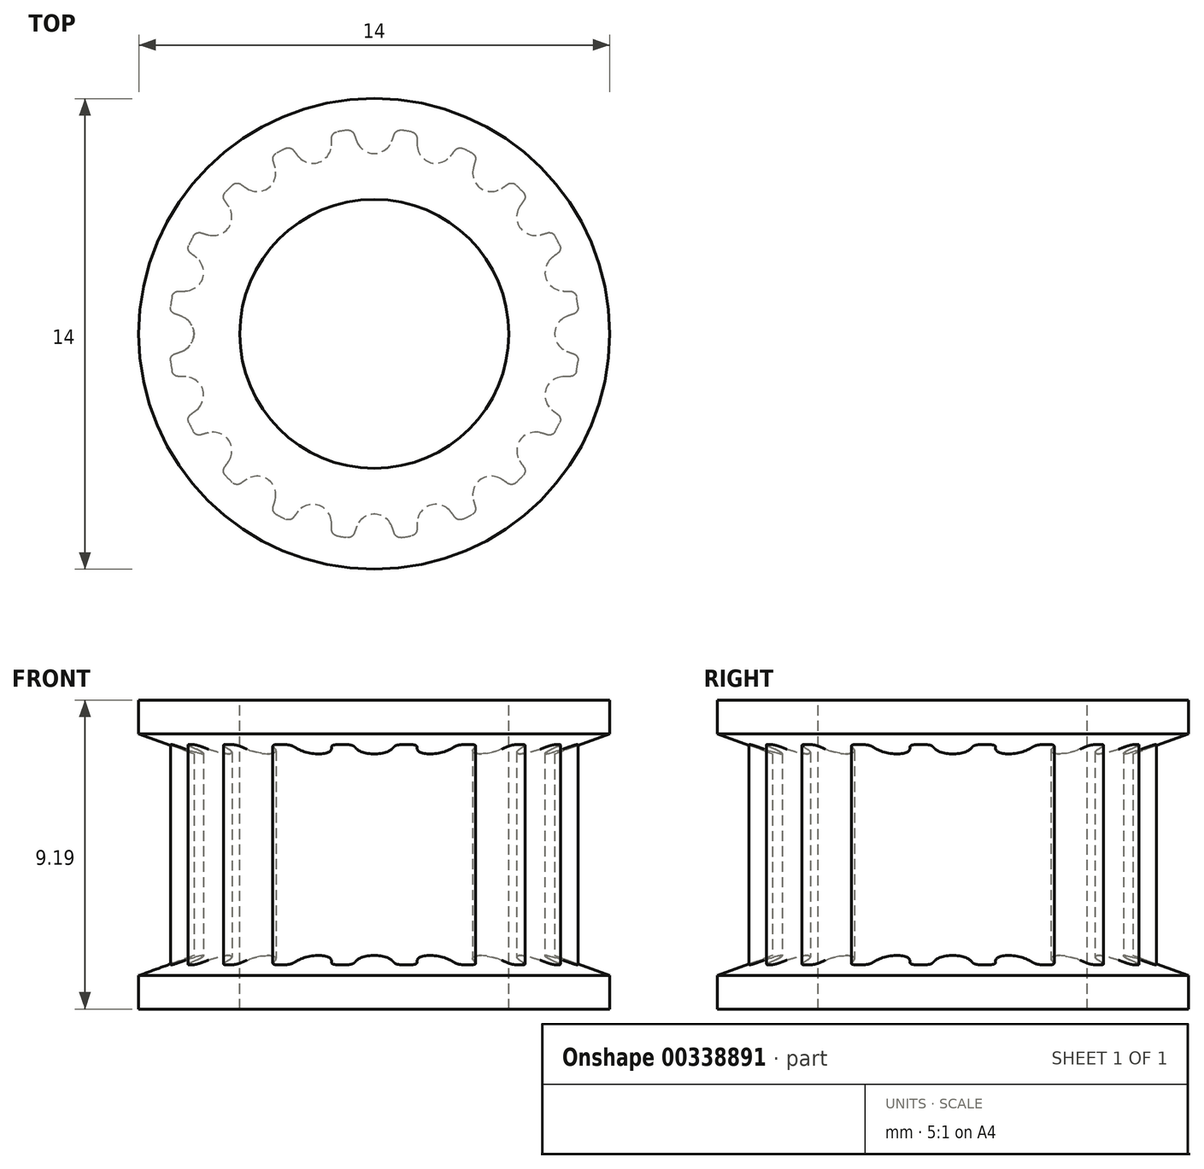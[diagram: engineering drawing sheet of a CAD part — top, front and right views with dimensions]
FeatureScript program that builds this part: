
annotation { "Feature Type Name" : "Feature", "Feature Type Description" : "" }
export const myFeature = defineFeature(function(context is Context, id is Id, definition is map)
    precondition{}
    {
        {
            assignVariable(context, id + "F0", {"name" : "teeth", "anyValue" : 20});
        }
        {
            assignVariable(context, id + "F1", {"name" : "total_length", "anyValue" : 9});
        }
        {
            var Q0;
            Q0=qCreatedBy(makeId("Top.planeOp"),FACE);
            var sketch = newSketch(context, id + "F2", { "sketchPlane" : qUnion([Q0])});
            skLineSegment(sketch, "E0", {"start": v(0, 0) * mm, "end": v(0, 5.36) * mm, "construction": true});
            skCircle(sketch, "E1", {"center": v(0, 0) * mm, "radius": 6.11 * mm});
            skPoint(sketch, "E2.MirrorCS.end.orphan", {"position": v(0.96, 6.04) * mm});
            skLineSegment(sketch, "E3", {"start": v(0.96, 6.04) * mm, "end": v(1, 6.29) * mm, "construction": true});
            skLineSegment(sketch, "E4", {"start": v(-0.96, 6.04) * mm, "end": v(-1, 6.29) * mm, "construction": true});
            skArc(sketch, "E5", {"start": v(0, 5.36) * mm, "mid": v(0.31, 5.46) * mm, "end": v(0.52, 5.72) * mm});
            skArc(sketch, "E6", {"start": v(0.52, 5.72) * mm, "mid": v(0.56, 5.83) * mm, "end": v(0.58, 5.94) * mm, "construction": true});
            skLineSegment(sketch, "E7", {"start": v(0, 5.36) * mm, "end": v(0, 6.11) * mm, "construction": true});
            skLineSegment(sketch, "E8", {"start": v(0, 6.11) * mm, "end": v(0, 6.37) * mm, "construction": true});
            skArc(sketch, "E9", {"start": v(0.58, 5.94) * mm, "mid": v(0.64, 6.04) * mm, "end": v(0.75, 6.07) * mm, "construction": true});
            skArc(sketch, "E10", {"start": v(1, 6.29) * mm, "mid": v(0, 6.37) * mm, "end": v(-1, 6.29) * mm, "construction": true});
            skLineSegment(sketch, "E11", {"start": v(0.96, 6.04) * mm, "end": v(0.84, 5.3) * mm});
            skLineSegment(sketch, "E12", {"start": v(0.84, 5.3) * mm, "end": v(0, 0) * mm});
            skLineSegment(sketch, "E13", {"start": v(0, 0) * mm, "end": v(-0.84, 5.3) * mm});
            skLineSegment(sketch, "E14", {"start": v(-0.84, 5.3) * mm, "end": v(-0.96, 6.04) * mm});
            skArc(sketch, "E15", {"start": v(0.8, 6.06) * mm, "mid": v(0.67, 6.03) * mm, "end": v(0.6, 5.93) * mm});
            skArc(sketch, "E16", {"start": v(0.52, 5.72) * mm, "mid": v(0.56, 5.83) * mm, "end": v(0.6, 5.93) * mm});
            skArc(sketch, "E17.MirrorCS", {"start": v(0, 5.36) * mm, "mid": v(-0.31, 5.46) * mm, "end": v(-0.52, 5.72) * mm});
            skArc(sketch, "E18.MirrorCS", {"start": v(-0.52, 5.72) * mm, "mid": v(-0.56, 5.83) * mm, "end": v(-0.6, 5.93) * mm});
            skArc(sketch, "E19.MirrorCS", {"start": v(-0.8, 6.06) * mm, "mid": v(-0.67, 6.03) * mm, "end": v(-0.6, 5.93) * mm});
            skArc(sketch, "E20", {"start": v(0, 6.11) * mm, "mid": v(-0.2, 6.1) * mm, "end": v(-0.4, 6.1) * mm});
            skArc(sketch, "E21", {"start": v(0.84, 5.3) * mm, "mid": v(0, 5.36) * mm, "end": v(-0.84, 5.3) * mm, "construction": true});
            skLineSegment(sketch, "E22", {"start": v(1, 6.29) * mm, "end": v(1.05, 6.66) * mm, "construction": true});
            skLineSegment(sketch, "E23", {"start": v(-1, 6.29) * mm, "end": v(-1.05, 6.66) * mm, "construction": true});
            skArc(sketch, "E24", {"start": v(-1.05, 6.66) * mm, "mid": v(0, 6.74) * mm, "end": v(1.05, 6.66) * mm, "construction": true});
            skSolve(sketch);
        }
        {
            var Q0;
            Q0=makeQuery(id+"F2.imprint","IMPRINT",FACE,{"disambiguationData":[TD([[makeQuery(id+"F2.imprint","IMPRINT",EDGE,{"derivedFrom":sQuery(id+"F2.wireOp",EDGE,"E5")}),-1.0]])]});
            var Q1;
            {var subQ1=sQuery(id+"F2.wireOp",EDGE,"E14");Q1=makeQuery(id+"F2.imprint","IMPRINT",FACE,{"disambiguationData":[TD([[makeQuery(id+"F2.imprint","IMPRINT",EDGE,{"derivedFrom":subQ1}),-1.0]])]});}
            var Q2;
            {var subQ0=sQuery(id+"F2.wireOp",EDGE,"E12");Q2=makeQuery(id+"F2.imprint","IMPRINT",FACE,{"disambiguationData":[TD([[makeQuery(id+"F2.imprint","IMPRINT",EDGE,{"derivedFrom":subQ0}),-1.0]])]});}
            extrude(context, id + "F3", {"entities" : qUnion([Q0, Q1, Q2]), "endBound" : BoundingType.SYMMETRIC, "depth" : (getVariable(context, 'total_length')) * mm});
        }
        {
            var Q0;
            Q0=makeQuery(id+"F3.opExtrude","SWEPT_BODY",BODY,{"disambiguationData":[OSD([sQuery(id+"F2.wireOp",EDGE,"E1"),sQuery(id+"F2.wireOp",EDGE,"E5"),sQuery(id+"F2.wireOp",EDGE,"E11"),sQuery(id+"F2.wireOp",EDGE,"E12"),sQuery(id+"F2.wireOp",EDGE,"E13"),sQuery(id+"F2.wireOp",EDGE,"E14"),sQuery(id+"F2.wireOp",EDGE,"E15"),sQuery(id+"F2.wireOp",EDGE,"E16"),sQuery(id+"F2.wireOp",EDGE,"E17.MirrorCS"),sQuery(id+"F2.wireOp",EDGE,"E18.MirrorCS"),sQuery(id+"F2.wireOp",EDGE,"E19.MirrorCS")])]});
            var Q1;
            Q1=makeQuery(id+"F3.opExtrude","SWEPT_EDGE",EDGE,{"disambiguationData":[OSD([sQuery(id+"F2.wireOp",EDGE,"E12"),sQuery(id+"F2.wireOp",EDGE,"E13")])]});
            circularPattern(context, id + "F4", {"operationType" : NewBodyOperationType.ADD, "entities" : qUnion([Q0]), "axis" : qUnion([Q1]), "angle" : 360 * degree, "instanceCount" : getVariable(context, 'teeth'), "equalSpace" : true});
        }
        {
            var Q0;
            Q0=qCreatedBy(makeId("Front.planeOp"),FACE);
            var sketch = newSketch(context, id + "F5", { "sketchPlane" : qUnion([Q0])});
            skLineSegment(sketch, "E25", {"start": v(0, 4.5) * mm, "end": v(7, 4.5) * mm});
            skLineSegment(sketch, "E26", {"start": v(7, 4.5) * mm, "end": v(7, 3.5) * mm});
            skLineSegment(sketch, "E27", {"start": v(7, 3.5) * mm, "end": v(5.36, 2.9) * mm});
            skLineSegment(sketch, "E28", {"start": v(5.36, 2.9) * mm, "end": v(0, 2.9) * mm});
            skLineSegment(sketch, "E29", {"start": v(0, 2.9) * mm, "end": v(0, 4.5) * mm});
            skLineSegment(sketch, "E30", {"start": v(0, -3.1) * mm, "end": v(5.36, -3.1) * mm});
            skLineSegment(sketch, "E31", {"start": v(5.36, -3.1) * mm, "end": v(7, -3.7) * mm});
            skLineSegment(sketch, "E32", {"start": v(7, -3.7) * mm, "end": v(7, -4.7) * mm});
            skLineSegment(sketch, "E33", {"start": v(7, -4.7) * mm, "end": v(0, -4.7) * mm});
            skLineSegment(sketch, "E34", {"start": v(0, -4.7) * mm, "end": v(0, -3.1) * mm});
            skSolve(sketch);
        }
        {
            var Q0;
            Q0=qSketchRegion(id+"F5",true);
            var Q1;
            Q1=sQuery(id+"F5.wireOp",EDGE,"E29");
            revolve(context, id + "F6", {"operationType" : NewBodyOperationType.ADD, "entities" : qUnion([Q0]), "axis" : qUnion([Q1]), "revolveType" : RevolveType.FULL});
        }
        {
            var Q0;
            Q0=qCreatedBy(makeId("Top.planeOp"),FACE);
            var sketch = newSketch(context, id + "F7", { "sketchPlane" : qUnion([Q0])});
            skCircle(sketch, "E35", {"center": v(0, 0) * mm, "radius": 4 * mm});
            skSolve(sketch);
        }
        {
            var Q0;
            Q0=qSketchRegion(id+"F7",true);
            extrude(context, id + "F8", {"entities" : qUnion([Q0]), "operationType" : NewBodyOperationType.REMOVE, "endBound" : BoundingType.SYMMETRIC, "oppositeDirection" : true, "depth" : 100 * mm});
        }
    });
